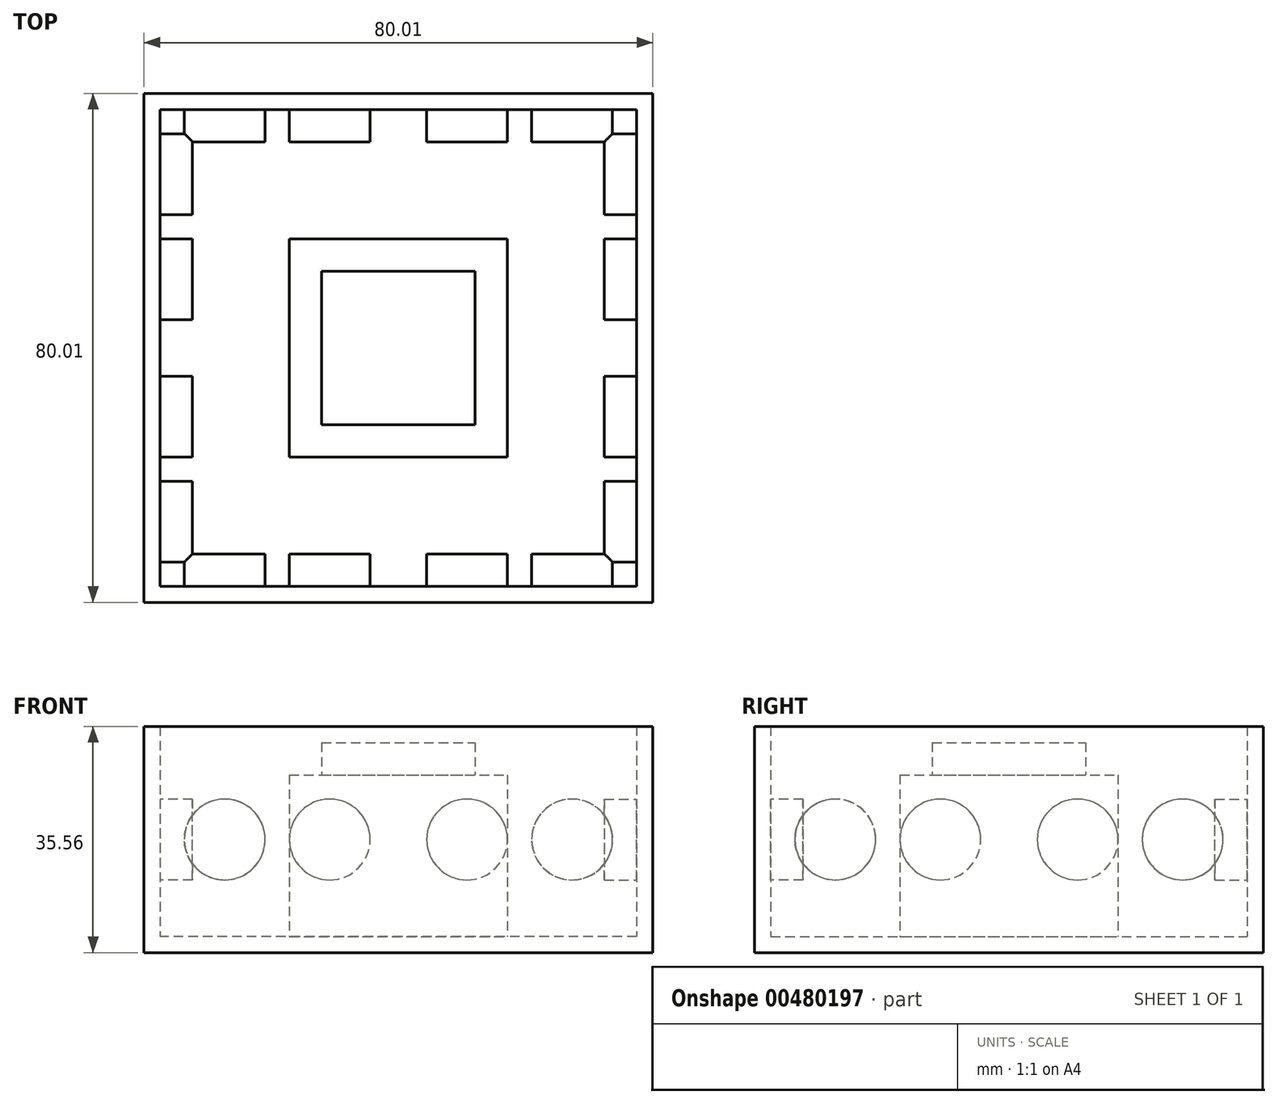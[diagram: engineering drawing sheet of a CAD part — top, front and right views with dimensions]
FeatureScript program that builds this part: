
annotation { "Feature Type Name" : "Feature", "Feature Type Description" : "" }
export const myFeature = defineFeature(function(context is Context, id is Id, definition is map)
    precondition{}
    {
        {
            var Q0;
            Q0=qCreatedBy(makeId("Top.planeOp"),FACE);
            var sketch = newSketch(context, id + "F0", { "sketchPlane" : qUnion([Q0])});
            skLineSegment(sketch, "E0.bottom", {"start": v(0, 0) * mm, "end": v(-80.01, 0) * mm});
            skLineSegment(sketch, "E0.top", {"start": v(0, 80.01) * mm, "end": v(-80.01, 80.01) * mm});
            skLineSegment(sketch, "E0.left", {"start": v(0, 0) * mm, "end": v(0, 80.01) * mm});
            skLineSegment(sketch, "E0.right", {"start": v(-80.01, 0) * mm, "end": v(-80.01, 80) * mm});
            skLineSegment(sketch, "E1.bottom", {"start": v(-5.08, 5.08) * mm, "end": v(-74.93, 5.08) * mm});
            skLineSegment(sketch, "E1.top", {"start": v(-5.08, 74.93) * mm, "end": v(-74.93, 74.93) * mm});
            skLineSegment(sketch, "E1.left", {"start": v(-5.08, 5.08) * mm, "end": v(-5.08, 74.93) * mm});
            skLineSegment(sketch, "E1.right", {"start": v(-74.93, 5.08) * mm, "end": v(-74.93, 74.93) * mm});
            skSolve(sketch);
        }
        {
            var Q0;
            Q0 = qSketchRegion(id + "F0", true);
            var Q1;
            Q1=makeQuery(id+"F0.imprint","IMPRINT",FACE,{"disambiguationData":[TD([[makeQuery(id+"F0.imprint","IMPRINT",EDGE,{"derivedFrom":sQuery(id+"F0.wireOp",EDGE,"E1.bottom")}),-1.0]])]});
            extrude(context, id + "F1", {"entities" : qUnion([Q0, Q1]), "depth" : 35.56 * mm});
        }
        {
            var Q0;
            Q0=makeQuery(id+"F1.opExtrude","CAP_FACE",FACE,{"disambiguationData":[OSD([sQuery(id+"F0.wireOp",EDGE,"E0.bottom"),sQuery(id+"F0.wireOp",EDGE,"E0.top"),sQuery(id+"F0.wireOp",EDGE,"E0.left"),sQuery(id+"F0.wireOp",EDGE,"E0.right")])],"isStart":false});
            shell(context, id + "F2", {"entities" : qUnion([Q0]), "thickness" : 2.54 * mm});
        }
        {
            var Q0;
            Q0=makeQuery(id+"F2.opShell","OFFSET_FACE",FACE,{"disambiguationData":[OSD([sQuery(id+"F0.wireOp",EDGE,"E0.bottom"),sQuery(id+"F0.wireOp",EDGE,"E0.top"),sQuery(id+"F0.wireOp",EDGE,"E0.left"),sQuery(id+"F0.wireOp",EDGE,"E0.right")])]});
            var sketch = newSketch(context, id + "F3", { "sketchPlane" : qUnion([Q0])});
            skLineSegment(sketch, "E2.bottom", {"start": v(-57.15, 22.86) * mm, "end": v(-22.86, 22.86) * mm});
            skLineSegment(sketch, "E2.top", {"start": v(-57.15, 57.15) * mm, "end": v(-22.86, 57.15) * mm});
            skLineSegment(sketch, "E2.left", {"start": v(-57.15, 22.86) * mm, "end": v(-57.15, 57.15) * mm});
            skLineSegment(sketch, "E2.right", {"start": v(-22.86, 22.86) * mm, "end": v(-22.86, 57.15) * mm});
            skLineSegment(sketch, "E3.bottom", {"start": v(-52.07, 27.94) * mm, "end": v(-27.94, 27.94) * mm});
            skLineSegment(sketch, "E3.top", {"start": v(-52.07, 52.07) * mm, "end": v(-27.94, 52.07) * mm});
            skLineSegment(sketch, "E3.left", {"start": v(-52.07, 27.94) * mm, "end": v(-52.07, 52.07) * mm});
            skLineSegment(sketch, "E3.right", {"start": v(-27.94, 27.94) * mm, "end": v(-27.94, 52.07) * mm});
            skSolve(sketch);
        }
        {
            var Q0;
            Q0=makeQuery(id+"F3.imprint","IMPRINT",FACE,{"disambiguationData":[TD([[makeQuery(id+"F3.imprint","IMPRINT",EDGE,{"derivedFrom":sQuery(id+"F3.wireOp",EDGE,"E2.bottom")}),1.0]])]});
            extrude(context, id + "F4", {"entities" : qUnion([Q0]), "operationType" : NewBodyOperationType.ADD, "depth" : 25.4 * mm});
        }
        {
            var Q0;
            Q0=makeQuery(id+"F4.boolean.opBoolean","SPLIT",FACE,{"disambiguationData":[TD([makeQuery(id+"F4.opExtrude","SWEPT_FACE",FACE,{"disambiguationData":[OSD([sQuery(id+"F3.wireOp",EDGE,"E3.bottom")])]})])],"derivedFrom":makeQuery(id+"F2.opShell","OFFSET_FACE",FACE,{"disambiguationData":[OSD([sQuery(id+"F0.wireOp",EDGE,"E0.bottom"),sQuery(id+"F0.wireOp",EDGE,"E0.top"),sQuery(id+"F0.wireOp",EDGE,"E0.left"),sQuery(id+"F0.wireOp",EDGE,"E0.right")])]})});
            extrude(context, id + "F5", {"entities" : qUnion([Q0]), "operationType" : NewBodyOperationType.ADD, "depth" : 30.48 * mm});
        }
        {
            var Q0;
            Q0=makeQuery(id+"F2.opShell","OFFSET_FACE",FACE,{"disambiguationData":[OSD([sQuery(id+"F0.wireOp",EDGE,"E0.top")])]});
            var sketch = newSketch(context, id + "F6", { "sketchPlane" : qUnion([Q0])});
            skCircle(sketch, "E4", {"center": v(-67.3, 17.78) * mm, "radius": 6.35 * mm});
            skCircle(sketch, "E5", {"center": v(-50.8, 17.78) * mm, "radius": 6.35 * mm});
            skCircle(sketch, "E6", {"center": v(-29.21, 17.78) * mm, "radius": 6.35 * mm});
            skCircle(sketch, "E7", {"center": v(-12.7, 17.78) * mm, "radius": 6.35 * mm});
            skSolve(sketch);
        }
        {
            var Q0;
            Q0=makeQuery(id+"F2.opShell","OFFSET_FACE",FACE,{"disambiguationData":[OSD([sQuery(id+"F0.wireOp",EDGE,"E0.left")])]});
            var sketch = newSketch(context, id + "F7", { "sketchPlane" : qUnion([Q0])});
            skCircle(sketch, "E8", {"center": v(-50.8, 17.78) * mm, "radius": 6.35 * mm});
            skCircle(sketch, "E9", {"center": v(-12.7, 17.78) * mm, "radius": 6.35 * mm});
            skCircle(sketch, "E10", {"center": v(-29.21, 17.78) * mm, "radius": 6.35 * mm});
            skCircle(sketch, "E11", {"center": v(-67.31, 17.78) * mm, "radius": 6.35 * mm});
            skSolve(sketch);
        }
        {
            var Q0;
            Q0=makeQuery(id+"F2.opShell","OFFSET_FACE",FACE,{"disambiguationData":[OSD([sQuery(id+"F0.wireOp",EDGE,"E0.bottom")])]});
            var sketch = newSketch(context, id + "F8", { "sketchPlane" : qUnion([Q0])});
            skCircle(sketch, "E12", {"center": v(12.7, 17.78) * mm, "radius": 6.35 * mm});
            skCircle(sketch, "E13", {"center": v(29.21, 17.78) * mm, "radius": 6.35 * mm});
            skCircle(sketch, "E14", {"center": v(50.8, 17.78) * mm, "radius": 6.35 * mm});
            skCircle(sketch, "E15", {"center": v(67.31, 17.78) * mm, "radius": 6.35 * mm});
            skSolve(sketch);
        }
        {
            var Q0;
            Q0=makeQuery(id+"F2.opShell","OFFSET_FACE",FACE,{"disambiguationData":[OSD([sQuery(id+"F0.wireOp",EDGE,"E0.right")])]});
            var sketch = newSketch(context, id + "F9", { "sketchPlane" : qUnion([Q0])});
            skCircle(sketch, "E16", {"center": v(12.7, 17.78) * mm, "radius": 6.35 * mm});
            skCircle(sketch, "E17", {"center": v(29.21, 17.78) * mm, "radius": 6.35 * mm});
            skCircle(sketch, "E18", {"center": v(67.31, 17.78) * mm, "radius": 6.35 * mm});
            skCircle(sketch, "E19", {"center": v(50.8, 17.78) * mm, "radius": 6.35 * mm});
            skSolve(sketch);
        }
        {
            var Q0;
            Q0=makeQuery(id+"F6.imprint","IMPRINT",FACE,{"disambiguationData":[TD([[makeQuery(id+"F6.imprint","IMPRINT",EDGE,{"derivedFrom":sQuery(id+"F6.wireOp",EDGE,"E7")}),1.0]])]});
            var Q1;
            Q1=makeQuery(id+"F6.imprint","IMPRINT",FACE,{"disambiguationData":[TD([[makeQuery(id+"F6.imprint","IMPRINT",EDGE,{"derivedFrom":sQuery(id+"F6.wireOp",EDGE,"E6")}),1.0]])]});
            var Q2;
            Q2=makeQuery(id+"F6.imprint","IMPRINT",FACE,{"disambiguationData":[TD([[makeQuery(id+"F6.imprint","IMPRINT",EDGE,{"derivedFrom":sQuery(id+"F6.wireOp",EDGE,"E5")}),1.0]])]});
            var Q3;
            Q3=makeQuery(id+"F6.imprint","IMPRINT",FACE,{"disambiguationData":[TD([[makeQuery(id+"F6.imprint","IMPRINT",EDGE,{"derivedFrom":sQuery(id+"F6.wireOp",EDGE,"E4")}),1.0]])]});
            extrude(context, id + "F10", {"entities" : qUnion([Q0, Q1, Q2, Q3]), "operationType" : NewBodyOperationType.ADD, "depth" : 5.08 * mm});
        }
        {
            var Q0;
            Q0=makeQuery(id+"F7.imprint","IMPRINT",FACE,{"disambiguationData":[TD([[makeQuery(id+"F7.imprint","IMPRINT",EDGE,{"derivedFrom":sQuery(id+"F7.wireOp",EDGE,"E9")}),1.0]])]});
            var Q1;
            Q1=makeQuery(id+"F7.imprint","IMPRINT",FACE,{"disambiguationData":[TD([[makeQuery(id+"F7.imprint","IMPRINT",EDGE,{"derivedFrom":sQuery(id+"F7.wireOp",EDGE,"E10")}),1.0]])]});
            var Q2;
            Q2=makeQuery(id+"F7.imprint","IMPRINT",FACE,{"disambiguationData":[TD([[makeQuery(id+"F7.imprint","IMPRINT",EDGE,{"derivedFrom":sQuery(id+"F7.wireOp",EDGE,"E8")}),1.0]])]});
            var Q3;
            Q3=makeQuery(id+"F7.imprint","IMPRINT",FACE,{"disambiguationData":[TD([[makeQuery(id+"F7.imprint","IMPRINT",EDGE,{"derivedFrom":sQuery(id+"F7.wireOp",EDGE,"E11")}),1.0]])]});
            extrude(context, id + "F11", {"entities" : qUnion([Q0, Q1, Q2, Q3]), "operationType" : NewBodyOperationType.ADD, "depth" : 5.08 * mm});
        }
        {
            var Q0;
            Q0=makeQuery(id+"F9.imprint","IMPRINT",FACE,{"disambiguationData":[TD([[makeQuery(id+"F9.imprint","IMPRINT",EDGE,{"derivedFrom":sQuery(id+"F9.wireOp",EDGE,"E18")}),1.0]])]});
            var Q1;
            Q1=makeQuery(id+"F9.imprint","IMPRINT",FACE,{"disambiguationData":[TD([[makeQuery(id+"F9.imprint","IMPRINT",EDGE,{"derivedFrom":sQuery(id+"F9.wireOp",EDGE,"E19")}),1.0]])]});
            var Q2;
            Q2=makeQuery(id+"F9.imprint","IMPRINT",FACE,{"disambiguationData":[TD([[makeQuery(id+"F9.imprint","IMPRINT",EDGE,{"derivedFrom":sQuery(id+"F9.wireOp",EDGE,"E17")}),1.0]])]});
            var Q3;
            Q3=makeQuery(id+"F9.imprint","IMPRINT",FACE,{"disambiguationData":[TD([[makeQuery(id+"F9.imprint","IMPRINT",EDGE,{"derivedFrom":sQuery(id+"F9.wireOp",EDGE,"E16")}),1.0]])]});
            extrude(context, id + "F12", {"entities" : qUnion([Q0, Q1, Q2, Q3]), "operationType" : NewBodyOperationType.ADD, "depth" : 5.08 * mm});
        }
        {
            var Q0;
            Q0=makeQuery(id+"F8.imprint","IMPRINT",FACE,{"disambiguationData":[TD([[makeQuery(id+"F8.imprint","IMPRINT",EDGE,{"derivedFrom":sQuery(id+"F8.wireOp",EDGE,"E13")}),1.0]])]});
            var Q1;
            Q1=makeQuery(id+"F8.imprint","IMPRINT",FACE,{"disambiguationData":[TD([[makeQuery(id+"F8.imprint","IMPRINT",EDGE,{"derivedFrom":sQuery(id+"F8.wireOp",EDGE,"E14")}),1.0]])]});
            var Q2;
            Q2=makeQuery(id+"F8.imprint","IMPRINT",FACE,{"disambiguationData":[TD([[makeQuery(id+"F8.imprint","IMPRINT",EDGE,{"derivedFrom":sQuery(id+"F8.wireOp",EDGE,"E15")}),1.0]])]});
            var Q3;
            Q3=makeQuery(id+"F8.imprint","IMPRINT",FACE,{"disambiguationData":[TD([[makeQuery(id+"F8.imprint","IMPRINT",EDGE,{"derivedFrom":sQuery(id+"F8.wireOp",EDGE,"E12")}),1.0]])]});
            extrude(context, id + "F13", {"entities" : qUnion([Q0, Q1, Q2, Q3]), "operationType" : NewBodyOperationType.ADD, "depth" : 5.08 * mm});
        }
    });
